# Revit family: Wall system Cementboard - Rigislab (STC 46_Uvalue 0.59)
name_source: partatom
category: Structural Stiffeners
units: mm (PartAtom-declared; Revit-internal decimal feet)

## family parameters
Cut with Voids When Loaded = No
OmniClass Number = 23.25.30.11.27
OmniClass Title = Vibration and Earthquake Controls
Shared = No

## types (1)
- STC 46(Cement board)
    Board 1 = Yes
    Board 2 = Yes
    Board Material = Cement Board
    Density = 20.00 kg/m³
    Description = Ecowool Rigislab is semi-rigid or rigid slabs of non-combustible, water repellent, glass mineral wool. They are designed to suit standard dry wall, ensuring a closed joint with adjacent slabs.
    ECOWOOL Product thickness in mm = 50
    Finish = BROWNIE RigiSlab
    Gypsum Thickness (mm) = 9 mm  [stored 0.0295276 ft]
    Height Wall (mm) = 2500 mm  [stored 8.2021 ft]
    Insulation Length (mm) = 609 mm  [stored 1.99803 ft]
    Insulation Thickness (mm) = 55 mm  [stored 0.180446 ft]
    Manufacturer = PGF Insulation Sdn. Bhd.
    Material Specification = Ecowool Brownie RigiSlab
    Metal Stud Spacer (mm) = 609 mm  [stored 1.99803 ft]
    Metal Stud Width = 64 mm  [stored 0.209974 ft]
    Remarks = Recommended for drywall partition applications where some acoustic performance
are required. Such as office & commercial environment
    STC No = 46
    STC in dB = 46
    System Description = 1. Cementboard-9mm
2. Ecowool Rigislab 50mm x 20kg/m3
3. Stud 64mm 
4. Cementboard-9mm
    Thermal K Value = 0.348
    Thermal R Value = 1.4
    Total System Thickness-mm = 82 mm  [stored 0.269029 ft]
    Type of Insulation = Glass Mineral Wool Semi-rigid slab
    U-Value (W/m2k) = 0.59

note: [stored X ft] marks values corroborated as IEEE doubles in the binary element streams (Revit-internal decimal feet)

## geometry (parser evidence)
native form markers: Sweep x17
no freeform markers — native parametric forms only
